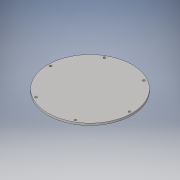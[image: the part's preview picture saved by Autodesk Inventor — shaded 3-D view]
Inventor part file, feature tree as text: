
AUTODESK INVENTOR PART (.ipt)
format: ipt  version: 2016 (Build 200138000, 138)  size: 98,816 bytes
history: native  units: in
note: dims shown in document units (in); Inventor stores cm internally (conversion verified against a paired STEP export)
features: extrude x1, sketch x1
ambient origin geometry x8: Origin, YZ Plane, XZ Plane, XY Plane, X Axis, Y Axis, Z Axis, Center Point
bodies: Solid1 (feature_tree)
feature tree (2):
  extrude  "Extrusion1"  Depth=0.108in
  sketch  "Sketch1"  dims[d0=4.63in d1=0.1181in d2=2.175in d3=2.3622in d5=360.0deg d7=0.108in d8=0.0in]
